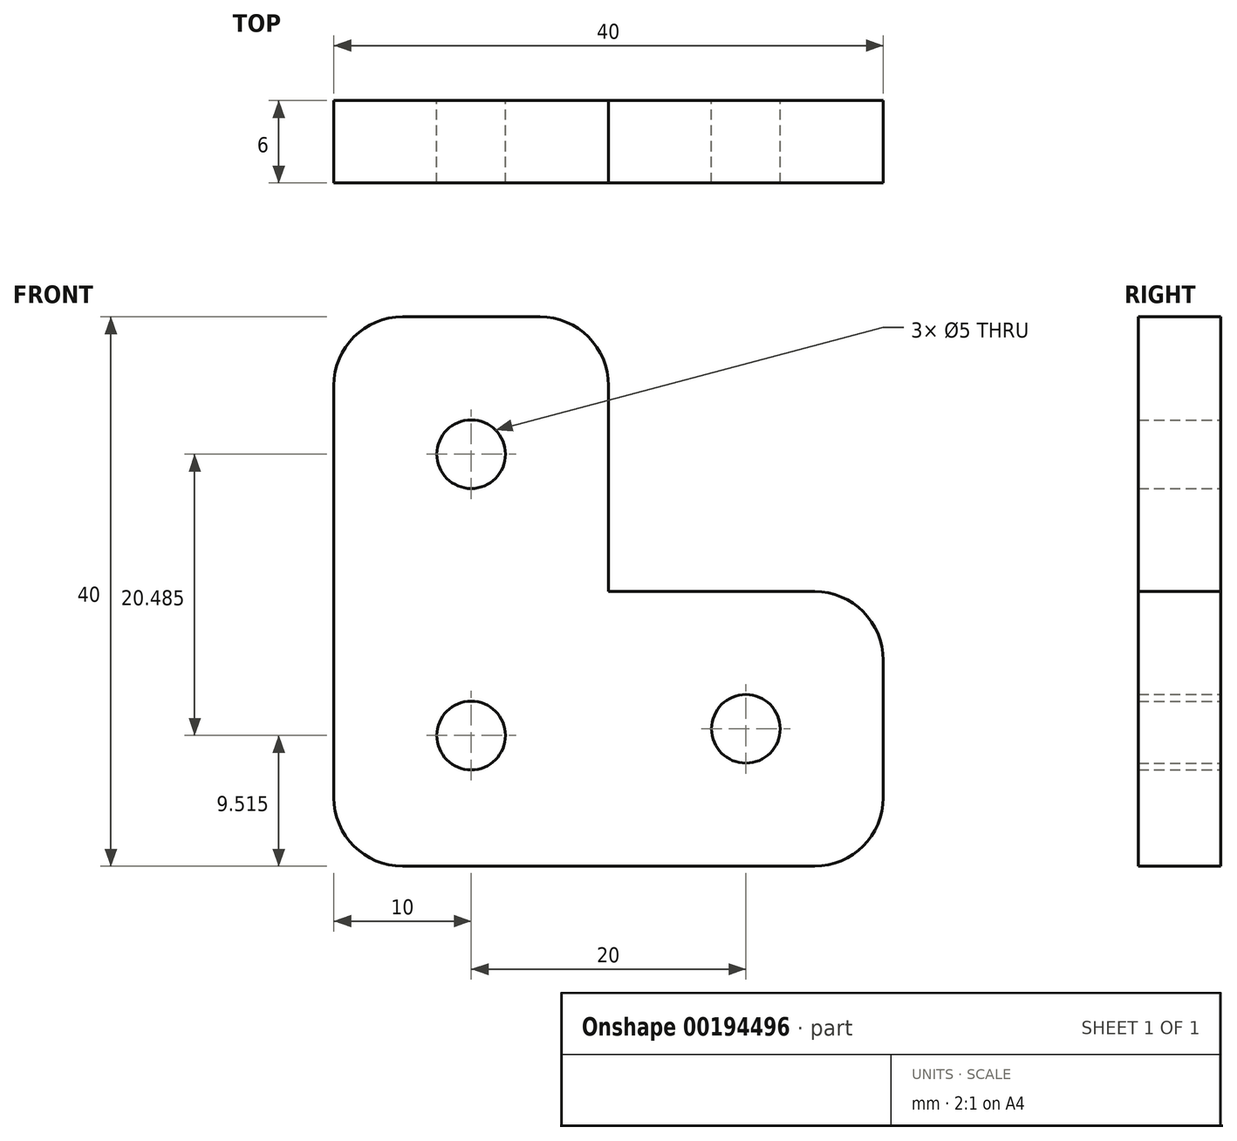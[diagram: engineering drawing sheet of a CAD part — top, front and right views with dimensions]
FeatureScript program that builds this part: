
annotation { "Feature Type Name" : "Feature", "Feature Type Description" : "" }
export const myFeature = defineFeature(function(context is Context, id is Id, definition is map)
    precondition{}
    {
        {
            var Q0;
            Q0=qCreatedBy(makeId("Front.planeOp"),FACE);
            var sketch = newSketch(context, id + "F0", { "sketchPlane" : qUnion([Q0])});
            skLineSegment(sketch, "E0", {"start": v(0, 0) * mm, "end": v(40, 0) * mm});
            skLineSegment(sketch, "E1", {"start": v(35, 0) * mm, "end": v(5, 0) * mm});
            skLineSegment(sketch, "E2", {"start": v(0, 5) * mm, "end": v(0, 35) * mm});
            skLineSegment(sketch, "E3", {"start": v(5, 40) * mm, "end": v(15, 40) * mm});
            skPoint(sketch, "E3.endSnap0", {"position": v(20, 0) * mm});
            skLineSegment(sketch, "E4", {"start": v(20, 35) * mm, "end": v(20, 20) * mm});
            skPoint(sketch, "E4.endSnap0", {"position": v(0, 20) * mm});
            skLineSegment(sketch, "E5", {"start": v(20, 20) * mm, "end": v(35, 20) * mm});
            skLineSegment(sketch, "E6", {"start": v(40, 15) * mm, "end": v(40, 5) * mm});
            skLineSegment(sketch, "E7", {"start": v(0, 20) * mm, "end": v(20, 20) * mm});
            skLineSegment(sketch, "E8", {"start": v(20, 20) * mm, "end": v(20, -0.97) * mm});
            skCircle(sketch, "E9", {"center": v(10, 9.52) * mm, "radius": 2.5 * mm});
            skPoint(sketch, "E9.centerSnap0", {"position": v(20, 9.52) * mm});
            skPoint(sketch, "E9.centerSnap1", {"position": v(10, 20) * mm});
            skCircle(sketch, "E10", {"center": v(10, 30) * mm, "radius": 2.5 * mm});
            skPoint(sketch, "E10.centerSnap0", {"position": v(10, 40) * mm});
            skPoint(sketch, "E10.centerSnap1", {"position": v(20, 30) * mm});
            skCircle(sketch, "E11", {"center": v(30, 10) * mm, "radius": 2.5 * mm});
            skPoint(sketch, "E11.centerSnap0", {"position": v(40, 10) * mm});
            skPoint(sketch, "E11.centerSnap1", {"position": v(30, 20) * mm});
            skPoint(sketch, "E12.visualSharp", {"position": v(0, 40) * mm});
            skArc(sketch, "E12.filletArc", {"start": v(5, 40) * mm, "mid": v(1.46, 38.54) * mm, "end": v(0, 35) * mm});
            skPoint(sketch, "E13.visualSharp", {"position": v(20, 40) * mm});
            skArc(sketch, "E13.filletArc", {"start": v(20, 35) * mm, "mid": v(18.54, 38.54) * mm, "end": v(15, 40) * mm});
            skPoint(sketch, "E14.visualSharp", {"position": v(0, 0) * mm});
            skArc(sketch, "E14.filletArc", {"start": v(0, 5) * mm, "mid": v(1.46, 1.46) * mm, "end": v(5, 0) * mm});
            skPoint(sketch, "E15.visualSharp", {"position": v(40, 0) * mm});
            skArc(sketch, "E15.filletArc", {"start": v(35, 0) * mm, "mid": v(38.54, 1.46) * mm, "end": v(40, 5) * mm});
            skPoint(sketch, "E16.visualSharp", {"position": v(40, 20) * mm});
            skArc(sketch, "E16.filletArc", {"start": v(40, 15) * mm, "mid": v(38.54, 18.54) * mm, "end": v(35, 20) * mm});
            skSolve(sketch);
        }
        {
            var Q0;
            {var subQ1=sQuery(id+"F0.wireOp",EDGE,"E7");Q0=makeQuery(id+"F0.imprint","IMPRINT",FACE,{"disambiguationData":[TD([[makeQuery(id+"F0.imprint","IMPRINT",EDGE,{"derivedFrom":subQ1}),-1.0]])]});}
            var Q1;
            Q1=makeQuery(id+"F0.imprint","IMPRINT",FACE,{"disambiguationData":[TD([[makeQuery(id+"F0.imprint","IMPRINT",EDGE,{"derivedFrom":sQuery(id+"F0.wireOp",EDGE,"E3")}),-1.0]])]});
            var Q2;
            {var subQ1=sQuery(id+"F0.wireOp",EDGE,"E5");Q2=makeQuery(id+"F0.imprint","IMPRINT",FACE,{"disambiguationData":[TD([[makeQuery(id+"F0.imprint","IMPRINT",EDGE,{"derivedFrom":subQ1}),-1.0]])]});}
            extrude(context, id + "F1", {"entities" : qUnion([Q0, Q1, Q2]), "depth" : 6 * mm});
        }
    });
